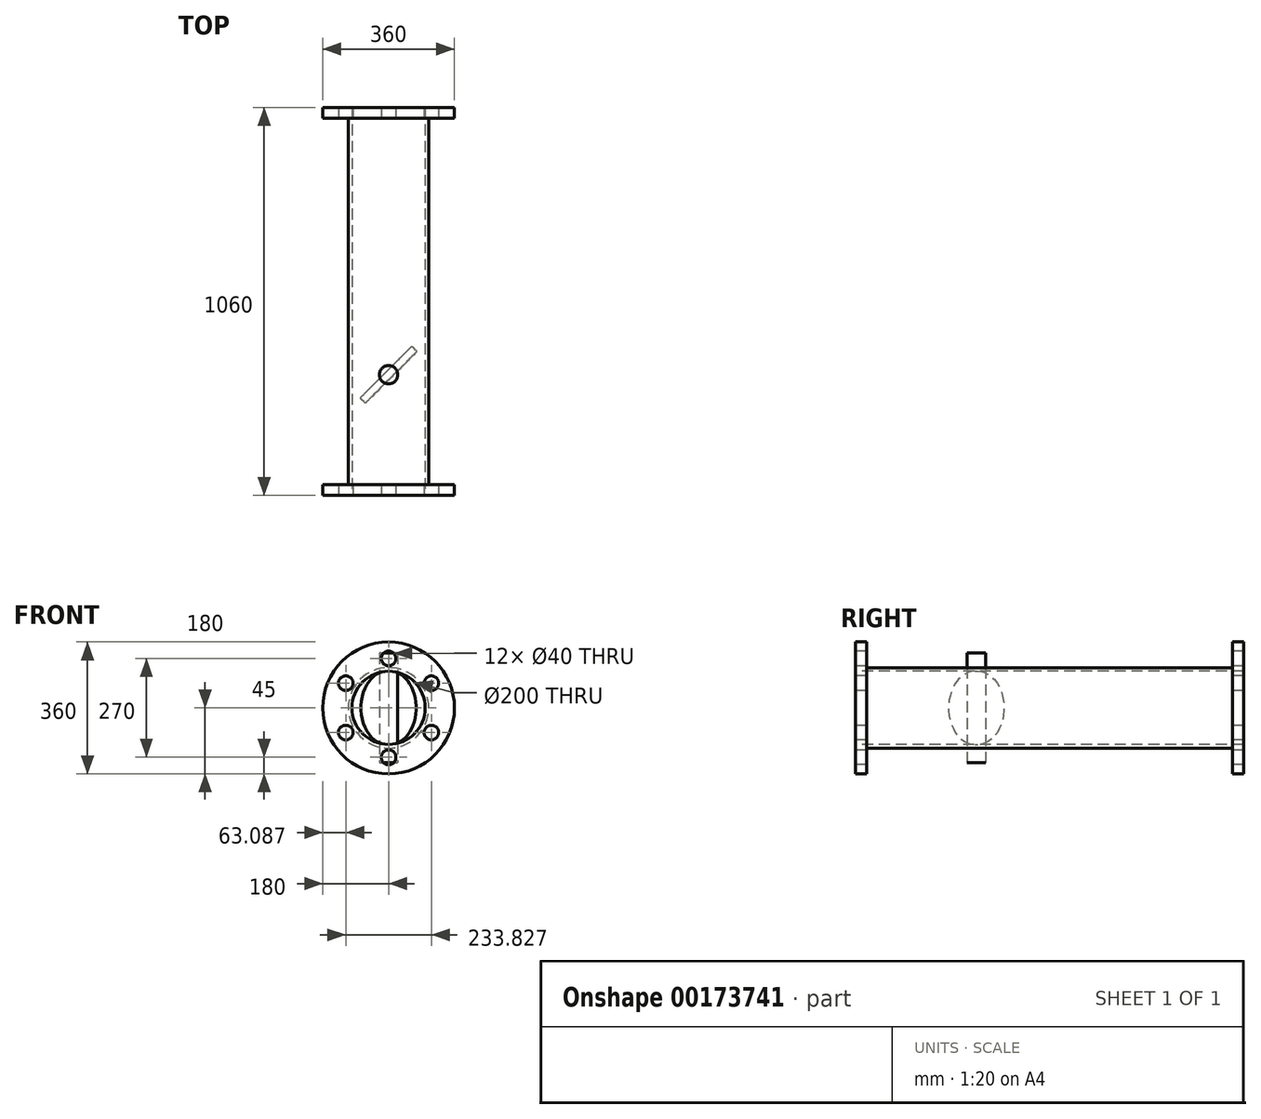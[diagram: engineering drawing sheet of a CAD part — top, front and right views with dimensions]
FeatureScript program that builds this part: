
annotation { "Feature Type Name" : "Feature", "Feature Type Description" : "" }
export const myFeature = defineFeature(function(context is Context, id is Id, definition is map)
    precondition{}
    {
        {
            var Q0;
            Q0=qCreatedBy(makeId("Front.planeOp"),FACE);
            var sketch = newSketch(context, id + "F0", { "sketchPlane" : qUnion([Q0])});
            skCircle(sketch, "E0", {"center": v(0, 0) * mm, "radius": 110 * mm});
            skSolve(sketch);
        }
        {
            var Q0;
            Q0 = qSketchRegion(id + "F0", true);
            extrude(context, id + "F1", {"entities" : qUnion([Q0]), "oppositeDirection" : true, "depth" : 1000 * mm});
        }
        {
            var Q0;
            Q0=makeQuery(id+"F1.opExtrude","CAP_FACE",FACE,{"disambiguationData":[OSD([sQuery(id+"F0.wireOp",EDGE,"E0")])],"isStart":true});
            var sketch = newSketch(context, id + "F2", { "sketchPlane" : qUnion([Q0])});
            skCircle(sketch, "E1", {"center": v(0, 0) * mm, "radius": 180 * mm});
            skSolve(sketch);
        }
        {
            var Q0;
            Q0 = qSketchRegion(id + "F2", true);
            extrude(context, id + "F3", {"entities" : qUnion([Q0]), "operationType" : NewBodyOperationType.ADD, "depth" : 30 * mm});
        }
        {
            var Q0;
            Q0=makeQuery(id+"F1.opExtrude","CAP_FACE",FACE,{"disambiguationData":[OSD([sQuery(id+"F0.wireOp",EDGE,"E0")])],"isStart":false});
            var sketch = newSketch(context, id + "F4", { "sketchPlane" : qUnion([Q0])});
            skCircle(sketch, "E2", {"center": v(0, 0) * mm, "radius": 180 * mm});
            skSolve(sketch);
        }
        {
            var Q0;
            Q0 = qSketchRegion(id + "F4", true);
            extrude(context, id + "F5", {"entities" : qUnion([Q0]), "operationType" : NewBodyOperationType.ADD, "depth" : 30 * mm});
        }
        {
            var Q0;
            Q0=makeQuery(id+"F3.opExtrude","CAP_FACE",FACE,{"disambiguationData":[OSD([sQuery(id+"F2.wireOp",EDGE,"E1")])],"isStart":false});
            var sketch = newSketch(context, id + "F6", { "sketchPlane" : qUnion([Q0])});
            skCircle(sketch, "E3", {"center": v(0, 0) * mm, "radius": 100 * mm});
            skSolve(sketch);
        }
        {
            var Q0;
            Q0=makeQuery(id+"F6.imprint","IMPRINT",FACE,{"disambiguationData":[TD([[makeQuery(id+"F6.imprint","IMPRINT",EDGE,{"derivedFrom":sQuery(id+"F6.wireOp",EDGE,"E3")}),1.0]])]});
            var Q1;
            Q1=makeQuery(id+"F5.opExtrude","CAP_FACE",FACE,{"disambiguationData":[OSD([sQuery(id+"F4.wireOp",EDGE,"E2")])],"isStart":false});
            extrude(context, id + "F7", {"entities" : qUnion([Q0]), "operationType" : NewBodyOperationType.REMOVE, "endBound" : BoundingType.UP_TO_SURFACE, "oppositeDirection" : true, "endBoundEntityFace" : qUnion([Q1]), "depth" : 25 * mm});
        }
        {
            var Q0;
            Q0=makeQuery(id+"F3.opExtrude","CAP_FACE",FACE,{"disambiguationData":[OSD([sQuery(id+"F2.wireOp",EDGE,"E1")])],"isStart":false});
            var sketch = newSketch(context, id + "F8", { "sketchPlane" : qUnion([Q0])});
            skCircle(sketch, "E4", {"center": v(0, 135) * mm, "radius": 20 * mm});
            skCircle(sketch, "E5.1.0", {"center": v(-116.91, 67.5) * mm, "radius": 20 * mm});
            skCircle(sketch, "E5.2.0", {"center": v(-116.91, -67.5) * mm, "radius": 20 * mm});
            skCircle(sketch, "E5.3.0", {"center": v(0, -135) * mm, "radius": 20 * mm});
            skCircle(sketch, "E5.4.0", {"center": v(116.91, -67.5) * mm, "radius": 20 * mm});
            skCircle(sketch, "E5.5.0", {"center": v(116.91, 67.5) * mm, "radius": 20 * mm});
            skPoint(sketch, "E5.center", {"position": v(0, 0) * mm});
            skSolve(sketch);
        }
        {
            var Q0;
            Q0 = qSketchRegion(id + "F8", true);
            var Q1;
            Q1=makeQuery(id+"F5.opExtrude","CAP_FACE",FACE,{"disambiguationData":[OSD([sQuery(id+"F4.wireOp",EDGE,"E2")])],"isStart":false});
            extrude(context, id + "F9", {"entities" : qUnion([Q0]), "operationType" : NewBodyOperationType.REMOVE, "endBound" : BoundingType.UP_TO_SURFACE, "oppositeDirection" : true, "endBoundEntityFace" : qUnion([Q1]), "depth" : 25 * mm});
        }
        {
            var Q0;
            Q0=qCreatedBy(makeId("Front.planeOp"),FACE);
            cPlane(context, id + "F10", {"entities" : qUnion([Q0]), "cplaneType" : CPlaneType.OFFSET, "offset" : 300 * mm, "oppositeDirection" : true, "width" : 150 * mm, "height" : 150 * mm});
        }
        {
            var Q0;
            Q0=qCreatedBy(id+"F10.planeOp",FACE);
            var sketch = newSketch(context, id + "F11", { "sketchPlane" : qUnion([Q0])});
            skCircle(sketch, "E6.0", {"center": v(0, 0) * mm, "radius": 100 * mm});
            skSolve(sketch);
        }
        {
            var Q0;
            Q0 = qSketchRegion(id + "F11", true);
            extrude(context, id + "F12", {"entities" : qUnion([Q0]), "depth" : 10 * mm, "hasSecondDirection" : true, "secondDirectionOppositeDirection" : true, "secondDirectionDepth" : 10 * mm});
        }
        {
            var Q0;
            Q0=makeQuery(id+"F12.opExtrude","CAP_EDGE",EDGE,{"disambiguationData":[OSD([sQuery(id+"F11.wireOp",EDGE,"E6.0")])],"isStart":false});
            var Q1;
            Q1=makeQuery(id+"F12.opExtrude","CAP_EDGE",EDGE,{"disambiguationData":[OSD([sQuery(id+"F11.wireOp",EDGE,"E6.0")])],"isStart":true});
            fillet(context, id + "F13", {"entities" : qUnion([Q0, Q1]), "radius" : 5 * mm, "tangentPropagation" : true, "allowEdgeOverflow" : false});
        }
        {
            var Q0;
            Q0=qCreatedBy(makeId("Top.planeOp"),FACE);
            var sketch = newSketch(context, id + "F14", { "sketchPlane" : qUnion([Q0])});
            skCircle(sketch, "E7", {"center": v(0, 300) * mm, "radius": 25 * mm});
            skSolve(sketch);
        }
        {
            var Q0;
            Q0 = qSketchRegion(id + "F14", true);
            extrude(context, id + "F15", {"entities" : qUnion([Q0]), "depth" : 300 * mm, "symmetric" : true});
        }
        {
            var Q0;
            Q0=qCreatedBy(makeId("Right.planeOp"),FACE);
            var sketch = newSketch(context, id + "F16", { "sketchPlane" : qUnion([Q0])});
            skPoint(sketch, "E8", {"position": v(300, 150) * mm});
            skLineSegment(sketch, "E9", {"start": v(300, 150) * mm, "end": v(300, -160.37) * mm, "construction": true});
            skSolve(sketch);
        }
        {
            var Q0;
            Q0=makeQuery(id+"F12.opExtrude","SWEPT_BODY",BODY,{"disambiguationData":[OSD([sQuery(id+"F11.wireOp",EDGE,"E6.0")])]});
            var Q1;
            Q1=sQuery(id+"F16.wireOp",EDGE,"E9");
            transform(context, id + "F17", {"entities" : qUnion([Q0]), "transformType" : TransformType.ROTATION, "transformAxis" : qUnion([Q1]), "angle" : 45 * degree, "oppositeDirection" : true, "makeCopy" : false});
        }
    });
